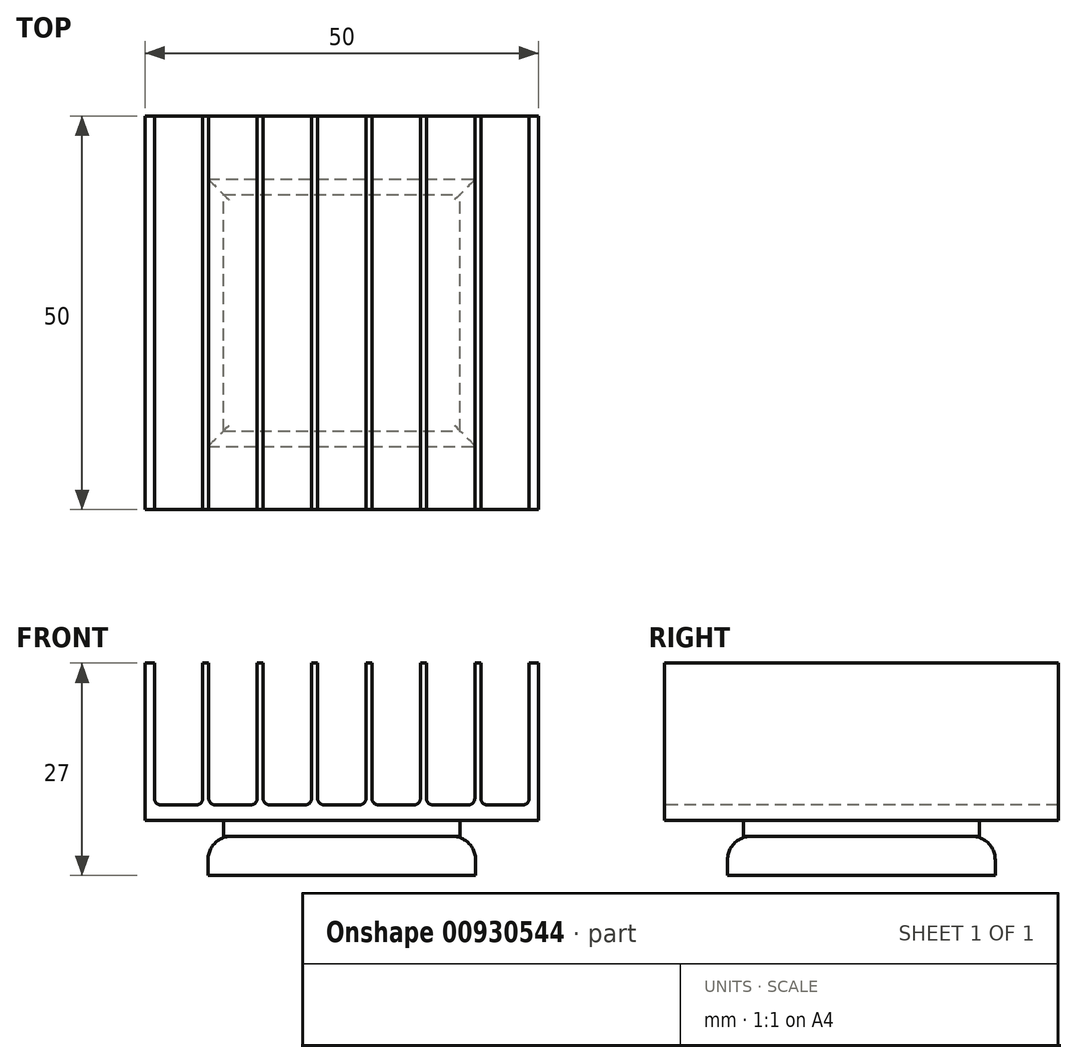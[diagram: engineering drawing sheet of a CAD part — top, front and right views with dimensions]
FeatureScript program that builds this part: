
annotation { "Feature Type Name" : "Feature", "Feature Type Description" : "" }
export const myFeature = defineFeature(function(context is Context, id is Id, definition is map)
    precondition{}
    {
        {
            var Q0;
            Q0=qCreatedBy(makeId("Front.planeOp"),FACE);
            var sketch = newSketch(context, id + "F0", { "sketchPlane" : qUnion([Q0])});
            skLineSegment(sketch, "E0.bottom", {"start": v(0, 20) * mm, "end": v(50, 20) * mm});
            skLineSegment(sketch, "E0.top", {"start": v(0, 0) * mm, "end": v(50, 0) * mm});
            skLineSegment(sketch, "E0.left", {"start": v(0, 20) * mm, "end": v(0, 0) * mm});
            skLineSegment(sketch, "E0.right", {"start": v(50, 20) * mm, "end": v(50, 0) * mm});
            skSolve(sketch);
        }
        {
            var Q0;
            Q0=qSketchRegion(id+"F0",true);
            extrude(context, id + "F1", {"entities" : qUnion([Q0]), "depth" : 50 * mm, "offsetDistance" : 25.4 * mm});
        }
        {
            var Q0;
            Q0=makeQuery(id+"F1.opExtrude","CAP_FACE",FACE,{"disambiguationData":[OSD([sQuery(id+"F0.wireOp",EDGE,"E0.bottom"),sQuery(id+"F0.wireOp",EDGE,"E0.top"),sQuery(id+"F0.wireOp",EDGE,"E0.left"),sQuery(id+"F0.wireOp",EDGE,"E0.right")])],"isStart":false});
            var sketch = newSketch(context, id + "F2", { "sketchPlane" : qUnion([Q0])});
            skLineSegment(sketch, "E1.bottom", {"start": v(48.8, 20) * mm, "end": v(42.66, 20) * mm});
            skLineSegment(sketch, "E1.top", {"start": v(48.8, 1.98) * mm, "end": v(42.66, 1.98) * mm});
            skLineSegment(sketch, "E1.left", {"start": v(48.8, 20) * mm, "end": v(48.8, 1.98) * mm});
            skLineSegment(sketch, "E1.right", {"start": v(42.66, 20) * mm, "end": v(42.66, 1.98) * mm});
            skLineSegment(sketch, "E2.bottom", {"start": v(41.9, 20) * mm, "end": v(35.75, 20) * mm});
            skLineSegment(sketch, "E2.top", {"start": v(41.9, 1.98) * mm, "end": v(35.75, 1.98) * mm});
            skLineSegment(sketch, "E2.left", {"start": v(41.9, 20) * mm, "end": v(41.9, 1.98) * mm});
            skLineSegment(sketch, "E2.right", {"start": v(35.75, 20) * mm, "end": v(35.75, 1.98) * mm});
            skLineSegment(sketch, "E3.bottom", {"start": v(34.98, 20) * mm, "end": v(28.84, 20) * mm});
            skLineSegment(sketch, "E3.top", {"start": v(34.98, 1.98) * mm, "end": v(28.84, 1.98) * mm});
            skLineSegment(sketch, "E3.left", {"start": v(34.98, 20) * mm, "end": v(34.98, 1.98) * mm});
            skLineSegment(sketch, "E3.right", {"start": v(28.84, 20) * mm, "end": v(28.84, 1.98) * mm});
            skLineSegment(sketch, "E4.bottom", {"start": v(28.07, 20) * mm, "end": v(21.93, 20) * mm});
            skLineSegment(sketch, "E4.top", {"start": v(28.07, 1.98) * mm, "end": v(21.93, 1.98) * mm});
            skLineSegment(sketch, "E4.left", {"start": v(28.07, 20) * mm, "end": v(28.07, 1.98) * mm});
            skLineSegment(sketch, "E4.right", {"start": v(21.93, 20) * mm, "end": v(21.93, 1.98) * mm});
            skLineSegment(sketch, "E5.bottom", {"start": v(21.16, 20) * mm, "end": v(15.02, 20) * mm});
            skLineSegment(sketch, "E5.top", {"start": v(21.16, 1.98) * mm, "end": v(15.02, 1.98) * mm});
            skLineSegment(sketch, "E5.left", {"start": v(21.16, 20) * mm, "end": v(21.16, 1.98) * mm});
            skLineSegment(sketch, "E5.right", {"start": v(15.02, 20) * mm, "end": v(15.02, 1.98) * mm});
            skLineSegment(sketch, "E6.bottom", {"start": v(14.25, 20) * mm, "end": v(8.1, 20) * mm});
            skLineSegment(sketch, "E6.top", {"start": v(14.25, 1.98) * mm, "end": v(8.1, 1.98) * mm});
            skLineSegment(sketch, "E6.left", {"start": v(14.25, 20) * mm, "end": v(14.25, 1.98) * mm});
            skLineSegment(sketch, "E6.right", {"start": v(8.1, 20) * mm, "end": v(8.1, 1.98) * mm});
            skLineSegment(sketch, "E7.bottom", {"start": v(7.34, 20) * mm, "end": v(1.2, 20) * mm});
            skLineSegment(sketch, "E7.top", {"start": v(7.34, 1.98) * mm, "end": v(1.2, 1.98) * mm});
            skLineSegment(sketch, "E7.left", {"start": v(7.34, 20) * mm, "end": v(7.34, 1.98) * mm});
            skLineSegment(sketch, "E7.right", {"start": v(1.2, 20) * mm, "end": v(1.2, 1.98) * mm});
            skSolve(sketch);
        }
        {
            var Q0;
            Q0=makeQuery(id+"F2.imprint","IMPRINT",FACE,{"disambiguationData":[TD([[makeQuery(id+"F2.imprint","IMPRINT",EDGE,{"derivedFrom":sQuery(id+"F2.wireOp",EDGE,"E7.bottom")}),-1.0]])]});
            var Q1;
            Q1=makeQuery(id+"F2.imprint","IMPRINT",FACE,{"disambiguationData":[TD([[makeQuery(id+"F2.imprint","IMPRINT",EDGE,{"derivedFrom":sQuery(id+"F2.wireOp",EDGE,"E6.bottom")}),-1.0]])]});
            var Q2;
            Q2=makeQuery(id+"F2.imprint","IMPRINT",FACE,{"disambiguationData":[TD([[makeQuery(id+"F2.imprint","IMPRINT",EDGE,{"derivedFrom":sQuery(id+"F2.wireOp",EDGE,"E5.bottom")}),-1.0]])]});
            var Q3;
            Q3=makeQuery(id+"F2.imprint","IMPRINT",FACE,{"disambiguationData":[TD([[makeQuery(id+"F2.imprint","IMPRINT",EDGE,{"derivedFrom":sQuery(id+"F2.wireOp",EDGE,"E4.bottom")}),-1.0]])]});
            var Q4;
            Q4=makeQuery(id+"F2.imprint","IMPRINT",FACE,{"disambiguationData":[TD([[makeQuery(id+"F2.imprint","IMPRINT",EDGE,{"derivedFrom":sQuery(id+"F2.wireOp",EDGE,"E3.bottom")}),-1.0]])]});
            var Q5;
            Q5=makeQuery(id+"F2.imprint","IMPRINT",FACE,{"disambiguationData":[TD([[makeQuery(id+"F2.imprint","IMPRINT",EDGE,{"derivedFrom":sQuery(id+"F2.wireOp",EDGE,"E2.bottom")}),-1.0]])]});
            var Q6;
            Q6=makeQuery(id+"F2.imprint","IMPRINT",FACE,{"disambiguationData":[TD([[makeQuery(id+"F2.imprint","IMPRINT",EDGE,{"derivedFrom":sQuery(id+"F2.wireOp",EDGE,"E1.bottom")}),-1.0]])]});
            extrude(context, id + "F3", {"entities" : qUnion([Q0, Q1, Q2, Q3, Q4, Q5, Q6]), "operationType" : NewBodyOperationType.REMOVE, "endBound" : BoundingType.THROUGH_ALL, "oppositeDirection" : true, "depth" : 25.4 * mm, "offsetDistance" : 25.4 * mm});
        }
        {
            var Q0;
            Q0=makeQuery(id+"F3.boolean.opBoolean","COPY",EDGE,{"derivedFrom":makeQuery(id+"F3.opExtrude","SWEPT_EDGE",EDGE,{"disambiguationData":[OSD([sQuery(id+"F2.wireOp",EDGE,"E7.top"),sQuery(id+"F2.wireOp",EDGE,"E7.right")])]})});
            var Q1;
            Q1=makeQuery(id+"F3.boolean.opBoolean","COPY",EDGE,{"derivedFrom":makeQuery(id+"F3.opExtrude","SWEPT_EDGE",EDGE,{"disambiguationData":[OSD([sQuery(id+"F2.wireOp",EDGE,"E7.top"),sQuery(id+"F2.wireOp",EDGE,"E7.left")])]})});
            var Q2;
            Q2=makeQuery(id+"F3.boolean.opBoolean","COPY",EDGE,{"derivedFrom":makeQuery(id+"F3.opExtrude","SWEPT_EDGE",EDGE,{"disambiguationData":[OSD([sQuery(id+"F2.wireOp",EDGE,"E6.top"),sQuery(id+"F2.wireOp",EDGE,"E6.right")])]})});
            var Q3;
            Q3=makeQuery(id+"F3.boolean.opBoolean","COPY",EDGE,{"derivedFrom":makeQuery(id+"F3.opExtrude","SWEPT_EDGE",EDGE,{"disambiguationData":[OSD([sQuery(id+"F2.wireOp",EDGE,"E6.top"),sQuery(id+"F2.wireOp",EDGE,"E6.left")])]})});
            var Q4;
            Q4=makeQuery(id+"F3.boolean.opBoolean","COPY",EDGE,{"derivedFrom":makeQuery(id+"F3.opExtrude","SWEPT_EDGE",EDGE,{"disambiguationData":[OSD([sQuery(id+"F2.wireOp",EDGE,"E5.top"),sQuery(id+"F2.wireOp",EDGE,"E5.right")])]})});
            var Q5;
            Q5=makeQuery(id+"F3.boolean.opBoolean","COPY",EDGE,{"derivedFrom":makeQuery(id+"F3.opExtrude","SWEPT_EDGE",EDGE,{"disambiguationData":[OSD([sQuery(id+"F2.wireOp",EDGE,"E5.top"),sQuery(id+"F2.wireOp",EDGE,"E5.left")])]})});
            var Q6;
            Q6=makeQuery(id+"F3.boolean.opBoolean","COPY",EDGE,{"derivedFrom":makeQuery(id+"F3.opExtrude","SWEPT_EDGE",EDGE,{"disambiguationData":[OSD([sQuery(id+"F2.wireOp",EDGE,"E4.top"),sQuery(id+"F2.wireOp",EDGE,"E4.right")])]})});
            var Q7;
            Q7=makeQuery(id+"F3.boolean.opBoolean","COPY",EDGE,{"derivedFrom":makeQuery(id+"F3.opExtrude","SWEPT_EDGE",EDGE,{"disambiguationData":[OSD([sQuery(id+"F2.wireOp",EDGE,"E4.top"),sQuery(id+"F2.wireOp",EDGE,"E4.left")])]})});
            var Q8;
            Q8=makeQuery(id+"F3.boolean.opBoolean","COPY",EDGE,{"derivedFrom":makeQuery(id+"F3.opExtrude","SWEPT_EDGE",EDGE,{"disambiguationData":[OSD([sQuery(id+"F2.wireOp",EDGE,"E3.top"),sQuery(id+"F2.wireOp",EDGE,"E3.right")])]})});
            var Q9;
            Q9=makeQuery(id+"F3.boolean.opBoolean","COPY",EDGE,{"derivedFrom":makeQuery(id+"F3.opExtrude","SWEPT_EDGE",EDGE,{"disambiguationData":[OSD([sQuery(id+"F2.wireOp",EDGE,"E3.top"),sQuery(id+"F2.wireOp",EDGE,"E3.left")])]})});
            var Q10;
            Q10=makeQuery(id+"F3.boolean.opBoolean","COPY",EDGE,{"derivedFrom":makeQuery(id+"F3.opExtrude","SWEPT_EDGE",EDGE,{"disambiguationData":[OSD([sQuery(id+"F2.wireOp",EDGE,"E2.top"),sQuery(id+"F2.wireOp",EDGE,"E2.right")])]})});
            var Q11;
            Q11=makeQuery(id+"F3.boolean.opBoolean","COPY",EDGE,{"derivedFrom":makeQuery(id+"F3.opExtrude","SWEPT_EDGE",EDGE,{"disambiguationData":[OSD([sQuery(id+"F2.wireOp",EDGE,"E2.top"),sQuery(id+"F2.wireOp",EDGE,"E2.left")])]})});
            var Q12;
            Q12=makeQuery(id+"F3.boolean.opBoolean","COPY",EDGE,{"derivedFrom":makeQuery(id+"F3.opExtrude","SWEPT_EDGE",EDGE,{"disambiguationData":[OSD([sQuery(id+"F2.wireOp",EDGE,"E1.top"),sQuery(id+"F2.wireOp",EDGE,"E1.right")])]})});
            var Q13;
            Q13=makeQuery(id+"F3.boolean.opBoolean","COPY",EDGE,{"derivedFrom":makeQuery(id+"F3.opExtrude","SWEPT_EDGE",EDGE,{"disambiguationData":[OSD([sQuery(id+"F2.wireOp",EDGE,"E1.top"),sQuery(id+"F2.wireOp",EDGE,"E1.left")])]})});
            fillet(context, id + "F4", {"entities" : qUnion([Q0, Q1, Q2, Q3, Q4, Q5, Q6, Q7, Q8, Q9, Q10, Q11, Q12, Q13]), "radius" : 0.8 * mm, "allowEdgeOverflow" : false});
        }
        {
            var Q0;
            Q0=makeQuery(id+"F1.opExtrude","SWEPT_FACE",FACE,{"disambiguationData":[OSD([sQuery(id+"F0.wireOp",EDGE,"E0.top")])]});
            var sketch = newSketch(context, id + "F5", { "sketchPlane" : qUnion([Q0])});
            skLineSegment(sketch, "E8.bottom", {"start": v(10, 40) * mm, "end": v(40, 40) * mm});
            skLineSegment(sketch, "E8.top", {"start": v(10, 10) * mm, "end": v(40, 10) * mm});
            skLineSegment(sketch, "E8.left", {"start": v(10, 40) * mm, "end": v(10, 10) * mm});
            skLineSegment(sketch, "E8.right", {"start": v(40, 40) * mm, "end": v(40, 10) * mm});
            skSolve(sketch);
        }
        {
            var Q0;
            Q0 = qSketchRegion(id + "F5", true);
            extrude(context, id + "F6", {"entities" : qUnion([Q0]), "depth" : 2 * mm, "offsetDistance" : 25.4 * mm});
        }
        {
            var Q0;
            Q0=makeQuery(id+"F6.opExtrude","CAP_FACE",FACE,{"disambiguationData":[OSD([sQuery(id+"F5.wireOp",EDGE,"E8.bottom"),sQuery(id+"F5.wireOp",EDGE,"E8.top"),sQuery(id+"F5.wireOp",EDGE,"E8.left"),sQuery(id+"F5.wireOp",EDGE,"E8.right")])],"isStart":false});
            var sketch = newSketch(context, id + "F7", { "sketchPlane" : qUnion([Q0])});
            skLineSegment(sketch, "E9.bottom", {"start": v(8, 42) * mm, "end": v(42, 42) * mm});
            skLineSegment(sketch, "E9.top", {"start": v(8, 8) * mm, "end": v(42, 8) * mm});
            skLineSegment(sketch, "E9.left", {"start": v(8, 42) * mm, "end": v(8, 8) * mm});
            skLineSegment(sketch, "E9.right", {"start": v(42, 42) * mm, "end": v(42, 8) * mm});
            skSolve(sketch);
        }
        {
            var Q0;
            Q0 = qSketchRegion(id + "F7", true);
            extrude(context, id + "F8", {"entities" : qUnion([Q0]), "depth" : 5 * mm, "offsetDistance" : 25.4 * mm});
        }
        {
            var Q0;
            Q0=makeQuery(id+"F8.opExtrude","CAP_EDGE",EDGE,{"disambiguationData":[OSD([sQuery(id+"F7.wireOp",EDGE,"E9.left")])],"isStart":true});
            var Q1;
            Q1=makeQuery(id+"F8.opExtrude","CAP_EDGE",EDGE,{"disambiguationData":[OSD([sQuery(id+"F7.wireOp",EDGE,"E9.bottom")])],"isStart":true});
            var Q2;
            Q2=makeQuery(id+"F8.opExtrude","CAP_EDGE",EDGE,{"disambiguationData":[OSD([sQuery(id+"F7.wireOp",EDGE,"E9.top")])],"isStart":true});
            var Q3;
            Q3=makeQuery(id+"F8.opExtrude","CAP_EDGE",EDGE,{"disambiguationData":[OSD([sQuery(id+"F7.wireOp",EDGE,"E9.right")])],"isStart":true});
            fillet(context, id + "F9", {"entities" : qUnion([Q0, Q1, Q2, Q3]), "radius" : 3 * mm, "tangentPropagation" : true, "allowEdgeOverflow" : false});
        }
    });
